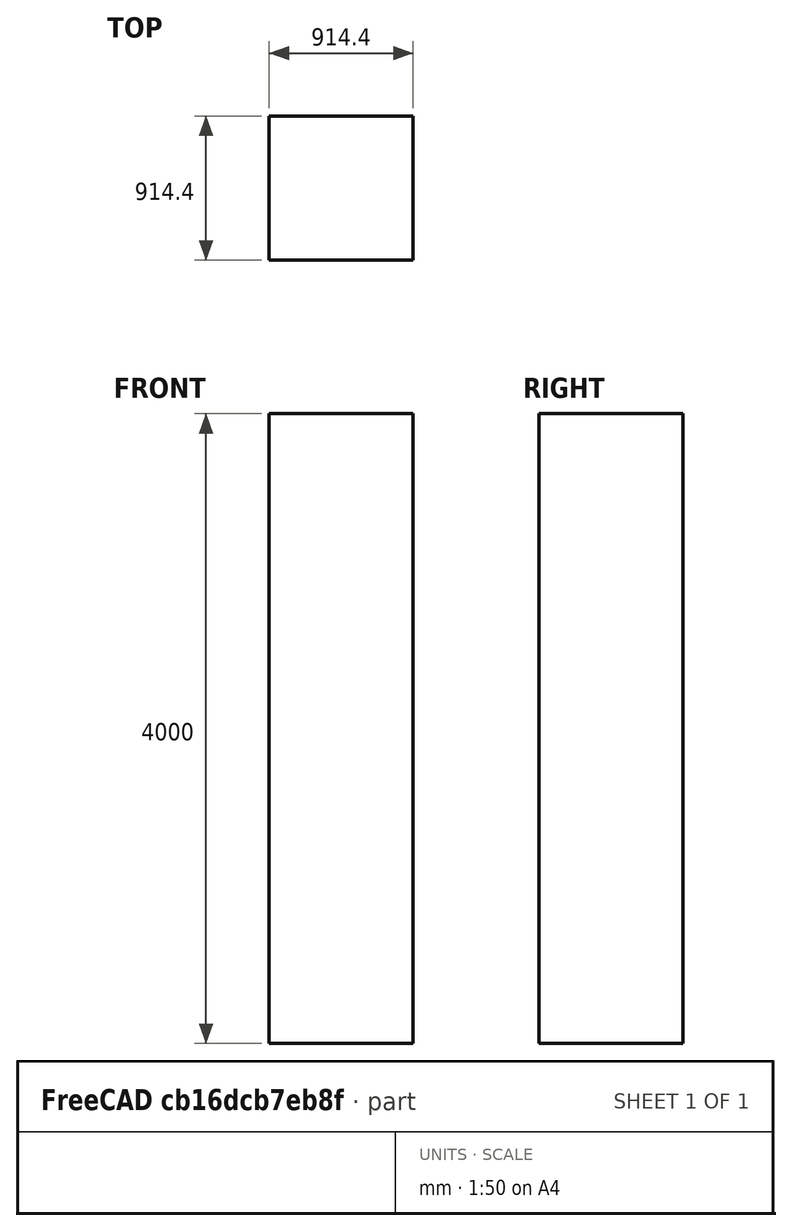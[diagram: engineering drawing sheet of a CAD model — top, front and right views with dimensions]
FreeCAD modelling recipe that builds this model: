
FCSTD DOCUMENT  (FreeCAD 1.0R39319 (Git))
Label: Box-VarSet-Example-v1
License: All rights reserved
LicenseURL: https://en.wikipedia.org/wiki/All_rights_reserved
objects: Part::Box×1, App::VarSet×1
note: 1 computed .brp shape members not serialized (recipe doc carries the construction recipe); baked Part::Feature solids carry a one-line shape summary decoded from their .brp

FEATURE [Part::Box] Box  label="Cube"
  AttacherType = Attacher::AttachEngine3D
  Height = 4000
  Length = 914.4
  Width = 914.4
  expr: Height = <<PQs>>.Height
  expr: Length = <<PQs>>.Length
  expr: Width = <<PQs>>.Width
FEATURE [App::VarSet] VarSet  label="PQs"
  CalcsLiveMappings = {\n  "docVersion": "0.2",\n  "unitsSchema": "UserPreferred",\n  "articleId": "3MAV4GNFQ-3FU",\n  "articleTitle": "calc for freecad demo 1: (LxWxH, rho) => (V, m)",\n  "lastUpdated": "2025-11-07T21:52:44.948Z",\n  "pqMappings": {\n    "Width": {\n      "symbol": "W",\n      "faceUnit": "m"\n    },\n    "Length": {\n      "symbol": "L",\n      "faceUnit": "m"\n    }\n  }\n}
  Height = 4000
  Length = 914.4
  Width = 914.4
